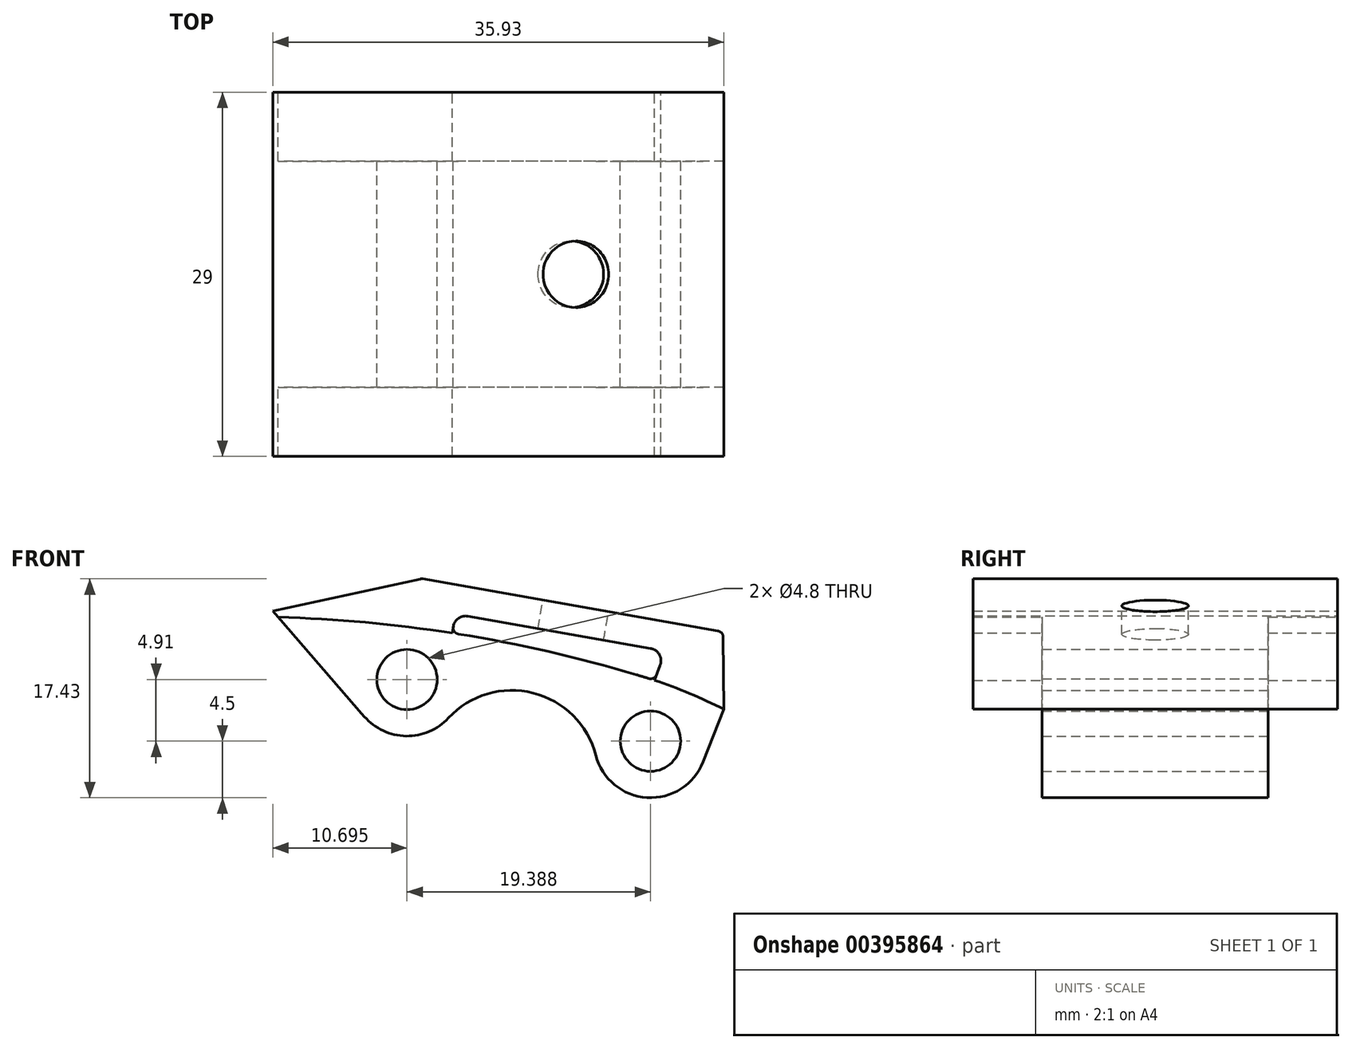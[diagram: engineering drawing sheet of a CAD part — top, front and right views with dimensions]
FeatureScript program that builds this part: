
annotation { "Feature Type Name" : "Feature", "Feature Type Description" : "" }
export const myFeature = defineFeature(function(context is Context, id is Id, definition is map)
    precondition{}
    {
        {
            var Q0;
            Q0=qCreatedBy(makeId("Front.planeOp"),FACE);
            var sketch = newSketch(context, id + "F0", { "sketchPlane" : qUnion([Q0])});
            skCircle(sketch, "E0", {"center": v(-8.96, -19.44) * mm, "radius": 2.4 * mm});
            skCircle(sketch, "E1", {"center": v(10.43, -24.35) * mm, "radius": 2.4 * mm});
            skLineSegment(sketch, "E2", {"start": v(-8.96, -19.44) * mm, "end": v(10.43, -24.35) * mm, "construction": true});
            skArc(sketch, "E3", {"start": v(-12.35, -22.4) * mm, "mid": v(-9.03, -23.94) * mm, "end": v(-5.66, -22.5) * mm});
            skArc(sketch, "E4", {"start": v(6.08, -25.48) * mm, "mid": v(10.16, -28.84) * mm, "end": v(14.62, -26) * mm});
            skArc(sketch, "E5", {"start": v(6.08, -25.48) * mm, "mid": v(1.09, -20.51) * mm, "end": v(-5.66, -22.5) * mm});
            skLineSegment(sketch, "E6", {"start": v(16.28, -21.8) * mm, "end": v(14.62, -26) * mm});
            skLineSegment(sketch, "E7", {"start": v(-19.65, -14) * mm, "end": v(-12.35, -22.4) * mm});
            skArc(sketch, "E8", {"start": v(9.31, -19.06) * mm, "mid": v(-4.81, -15.83) * mm, "end": v(-19.23, -14.48) * mm});
            skPoint(sketch, "E9.center.orphan", {"position": v(-3.72, -31.83) * mm});
            skArc(sketch, "E10", {"start": v(16.28, -21.8) * mm, "mid": v(12.86, -20.27) * mm, "end": v(9.31, -19.06) * mm});
            skLineSegment(sketch, "E11", {"start": v(11.2, -18.31) * mm, "end": v(10.73, -19.5) * mm});
            skLineSegment(sketch, "E12", {"start": v(10.44, -16.96) * mm, "end": v(-4.1, -14.4) * mm});
            skLineSegment(sketch, "E13", {"start": v(-5.27, -15.2) * mm, "end": v(-5.36, -15.74) * mm});
            skLineSegment(sketch, "E14", {"start": v(11.65, -17.18) * mm, "end": v(11.69, -16.98) * mm, "construction": true});
            skLineSegment(sketch, "E15", {"start": v(16.24, -17.78) * mm, "end": v(-13.2, -12.6) * mm, "construction": true});
            skLineSegment(sketch, "E16", {"start": v(-7.8, -11.41) * mm, "end": v(16.21, -15.64) * mm});
            skPoint(sketch, "E17.visualSharp", {"position": v(-5.1, -14.22) * mm});
            skArc(sketch, "E17.filletArc", {"start": v(-4.1, -14.4) * mm, "mid": v(-4.85, -14.56) * mm, "end": v(-5.27, -15.2) * mm});
            skPoint(sketch, "E18.visualSharp", {"position": v(11.65, -17.18) * mm});
            skArc(sketch, "E18.filletArc", {"start": v(11.2, -18.31) * mm, "mid": v(11.14, -17.46) * mm, "end": v(10.44, -16.96) * mm});
            skLineSegment(sketch, "E19", {"start": v(-19.65, -14) * mm, "end": v(-7.8, -11.41) * mm});
            skLineSegment(sketch, "E20", {"start": v(16.21, -15.64) * mm, "end": v(16.28, -21.8) * mm});
            skSolve(sketch);
        }
        {
            var Q0;
            Q0=qSketchRegion(id+"F0",true);
            extrude(context, id + "F1", {"entities" : qUnion([Q0]), "endBound" : BoundingType.SYMMETRIC, "depth" : 18 * mm});
        }
        {
            var Q0;
            {var subQ3=sQuery(id+"F0.wireOp",EDGE,"E11");Q0=makeQuery(id+"F0.imprint","IMPRINT",FACE,{"disambiguationData":[TD([[makeQuery(id+"F0.imprint","IMPRINT",EDGE,{"derivedFrom":subQ3}),1.0]])]});}
            extrude(context, id + "F2", {"entities" : qUnion([Q0]), "operationType" : NewBodyOperationType.ADD, "endBound" : BoundingType.SYMMETRIC, "depth" : 29 * mm});
        }
        {
            var Q0;
            Q0=makeQuery(id+"F1.opExtrude","SWEPT_EDGE",EDGE,{"disambiguationData":[OSD([sQuery(id+"F0.wireOp",EDGE,"E8"),sQuery(id+"F0.wireOp",EDGE,"75ewls0l-BJo7-nbw7-1Z3j-4MJ6eTp4PVSf")])]});
            var Q1;
            {var subQ0=sQuery(id+"F0.wireOp",EDGE,"E11");var subQ1=sQuery(id+"F0.wireOp",EDGE,"75ewls0l-BJo7-nbw7-1Z3j-4MJ6eTp4PVSf");Q1=makeQuery(id+"F2.boolean.opBoolean","MERGE",EDGE,{"derivedFrom":[makeQuery(id+"F1.opExtrude","SWEPT_EDGE",EDGE,{"disambiguationData":[OSD([subQ1,subQ0])]}),makeQuery(id+"F2.opExtrude","SWEPT_EDGE",EDGE,{"disambiguationData":[OSD([subQ1,subQ0])]})]});}
            var Q2;
            Q2=makeQuery(id+"F1.opExtrude","SWEPT_EDGE",EDGE,{"disambiguationData":[OSD([sQuery(id+"F0.wireOp",EDGE,"E10"),sQuery(id+"F0.wireOp",EDGE,"E11")])]});
            fillet(context, id + "F3", {"entities" : qUnion([Q0, Q1, Q2]), "radius" : 0.5 * mm, "tangentPropagation" : true, "allowEdgeOverflow" : false});
        }
        {
            var Q0;
            {var subQ0=sQuery(id+"F0.wireOp",EDGE,"E16");Q0=makeQuery(id+"F2.boolean.opBoolean","MERGE",FACE,{"derivedFrom":[makeQuery(id+"F1.opExtrude","SWEPT_FACE",FACE,{"disambiguationData":[OSD([subQ0])]}),makeQuery(id+"F2.opExtrude","SWEPT_FACE",FACE,{"disambiguationData":[OSD([subQ0])]})]});}
            var sketch = newSketch(context, id + "F4", { "sketchPlane" : qUnion([Q0])});
            skCircle(sketch, "E21", {"center": v(6.77, 0) * mm, "radius": 2.65 * mm});
            skSolve(sketch);
        }
        {
            var Q0;
            Q0=makeQuery(id+"F4.imprint","IMPRINT",FACE,{"disambiguationData":[TD([[makeQuery(id+"F4.imprint","IMPRINT",EDGE,{"derivedFrom":sQuery(id+"F4.wireOp",EDGE,"E21")}),1.0]])]});
            extrude(context, id + "F5", {"entities" : qUnion([Q0]), "operationType" : NewBodyOperationType.REMOVE, "oppositeDirection" : true, "depth" : 3 * mm});
        }
        {
            var Q0;
            {var subQ0=sQuery(id+"F0.wireOp",EDGE,"E19");var subQ1=sQuery(id+"F0.wireOp",EDGE,"E16");Q0=makeQuery(id+"F2.boolean.opBoolean","MERGE",EDGE,{"derivedFrom":[makeQuery(id+"F1.opExtrude","SWEPT_EDGE",EDGE,{"disambiguationData":[OSD([subQ1,subQ0])]}),makeQuery(id+"F2.opExtrude","SWEPT_EDGE",EDGE,{"disambiguationData":[OSD([subQ1,subQ0])]})]});}
            var Q1;
            {var subQ0=sQuery(id+"F0.wireOp",EDGE,"E20");var subQ1=sQuery(id+"F0.wireOp",EDGE,"E16");Q1=makeQuery(id+"F2.boolean.opBoolean","MERGE",EDGE,{"derivedFrom":[makeQuery(id+"F1.opExtrude","SWEPT_EDGE",EDGE,{"disambiguationData":[OSD([subQ1,subQ0])]}),makeQuery(id+"F2.opExtrude","SWEPT_EDGE",EDGE,{"disambiguationData":[OSD([subQ1,subQ0])]})]});}
            fillet(context, id + "F6", {"entities" : qUnion([Q0, Q1]), "radius" : 0.5 * mm, "tangentPropagation" : true, "allowEdgeOverflow" : false});
        }
    });
